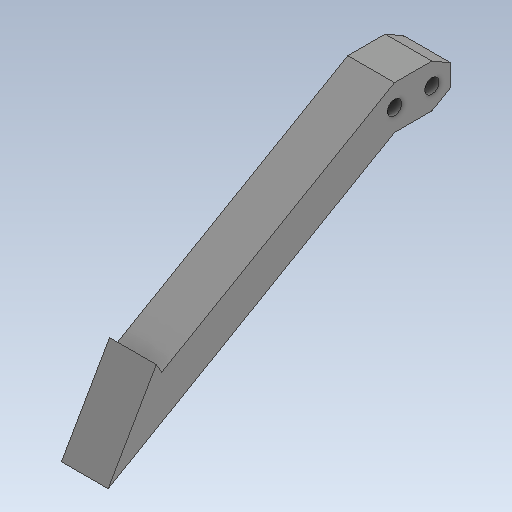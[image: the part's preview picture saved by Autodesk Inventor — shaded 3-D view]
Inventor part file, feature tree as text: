
AUTODESK INVENTOR PART (.ipt)
format: ipt  version: 2020 (Build 240168000, 168)  size: 153,600 bytes
history: native  units: in
note: dims shown in document units (in); Inventor stores cm internally (conversion verified against a paired STEP export)
features: extrude x1, sketch x1
ambient origin geometry x8: Origin, YZ Plane, XZ Plane, XY Plane, X Axis, Y Axis, Z Axis, Center Point
bodies: Body1 (feature_tree)
feature tree (2):
  extrude  "Extrusion2"  Depth=0.3937in
  sketch  "Sketch1"  dims[d3=0.1818in d4=0.6299in d15=0.315in d16=0.315in d18=0.122in d19=0.122in d20=0.1818in d23=0.0787in d24=1.5752in d25=60.0deg d26=30.0deg d27=2.8858in d32=0.3937in d33=0.0in]
